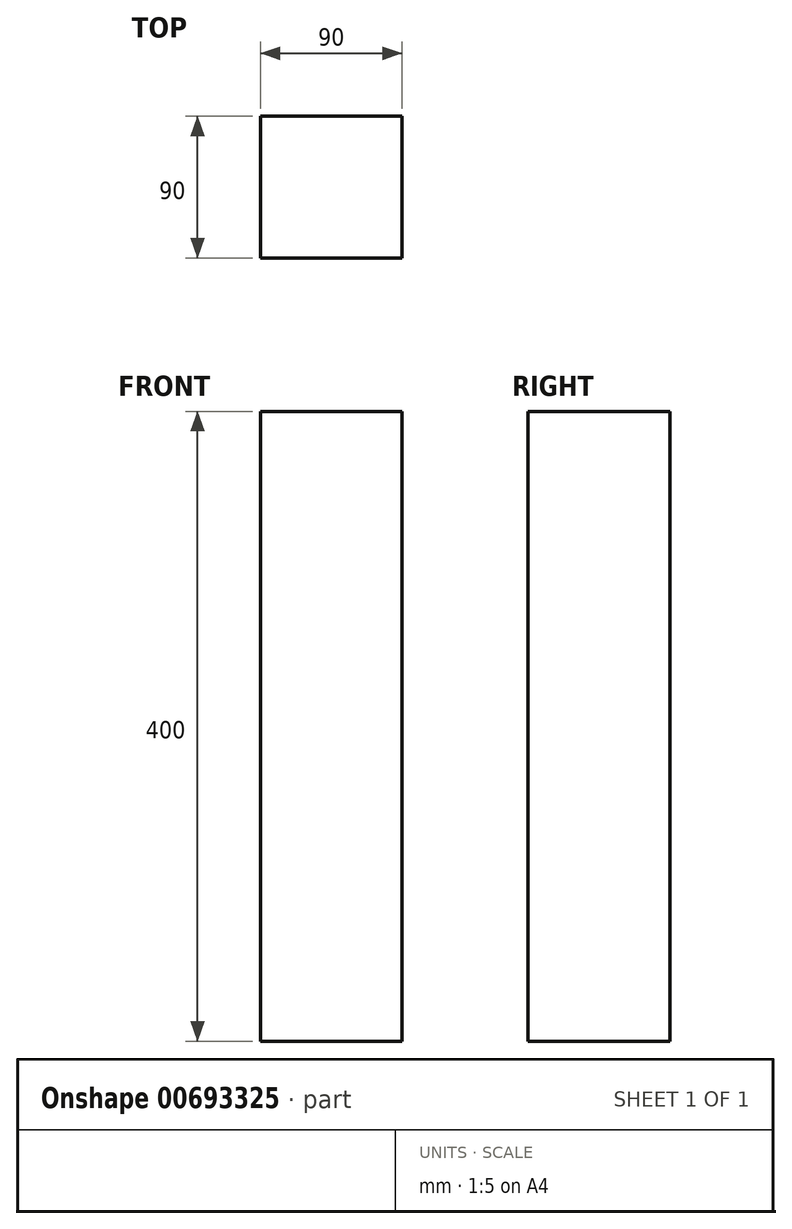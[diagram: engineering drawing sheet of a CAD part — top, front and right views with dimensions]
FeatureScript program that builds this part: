
annotation { "Feature Type Name" : "Feature", "Feature Type Description" : "" }
export const myFeature = defineFeature(function(context is Context, id is Id, definition is map)
    precondition{}
    {
        {
            var Q0;
            Q0=qCreatedBy(makeId("Top.planeOp"),FACE);
            var sketch = newSketch(context, id + "F0", { "sketchPlane" : qUnion([Q0])});
            skLineSegment(sketch, "E0.bottom", {"start": v(45, -45) * mm, "end": v(-45, -45) * mm});
            skLineSegment(sketch, "E0.top", {"start": v(45, 45) * mm, "end": v(-45, 45) * mm});
            skLineSegment(sketch, "E0.left", {"start": v(45, -45) * mm, "end": v(45, 45) * mm});
            skLineSegment(sketch, "E0.right", {"start": v(-45, -45) * mm, "end": v(-45, 45) * mm});
            skPoint(sketch, "E0.middle", {"position": v(0, 0) * mm});
            skSolve(sketch);
        }
        {
            var Q0;
            Q0=makeQuery(id+"F0.imprint","IMPRINT",FACE,{"disambiguationData":[TD([[makeQuery(id+"F0.imprint","IMPRINT",EDGE,{"derivedFrom":sQuery(id+"F0.wireOp",EDGE,"E0.bottom")}),-1.0]])]});
            extrude(context, id + "F1", {"entities" : qUnion([Q0]), "depth" : 400 * mm, "offsetDistance" : 25 * mm});
        }
    });
